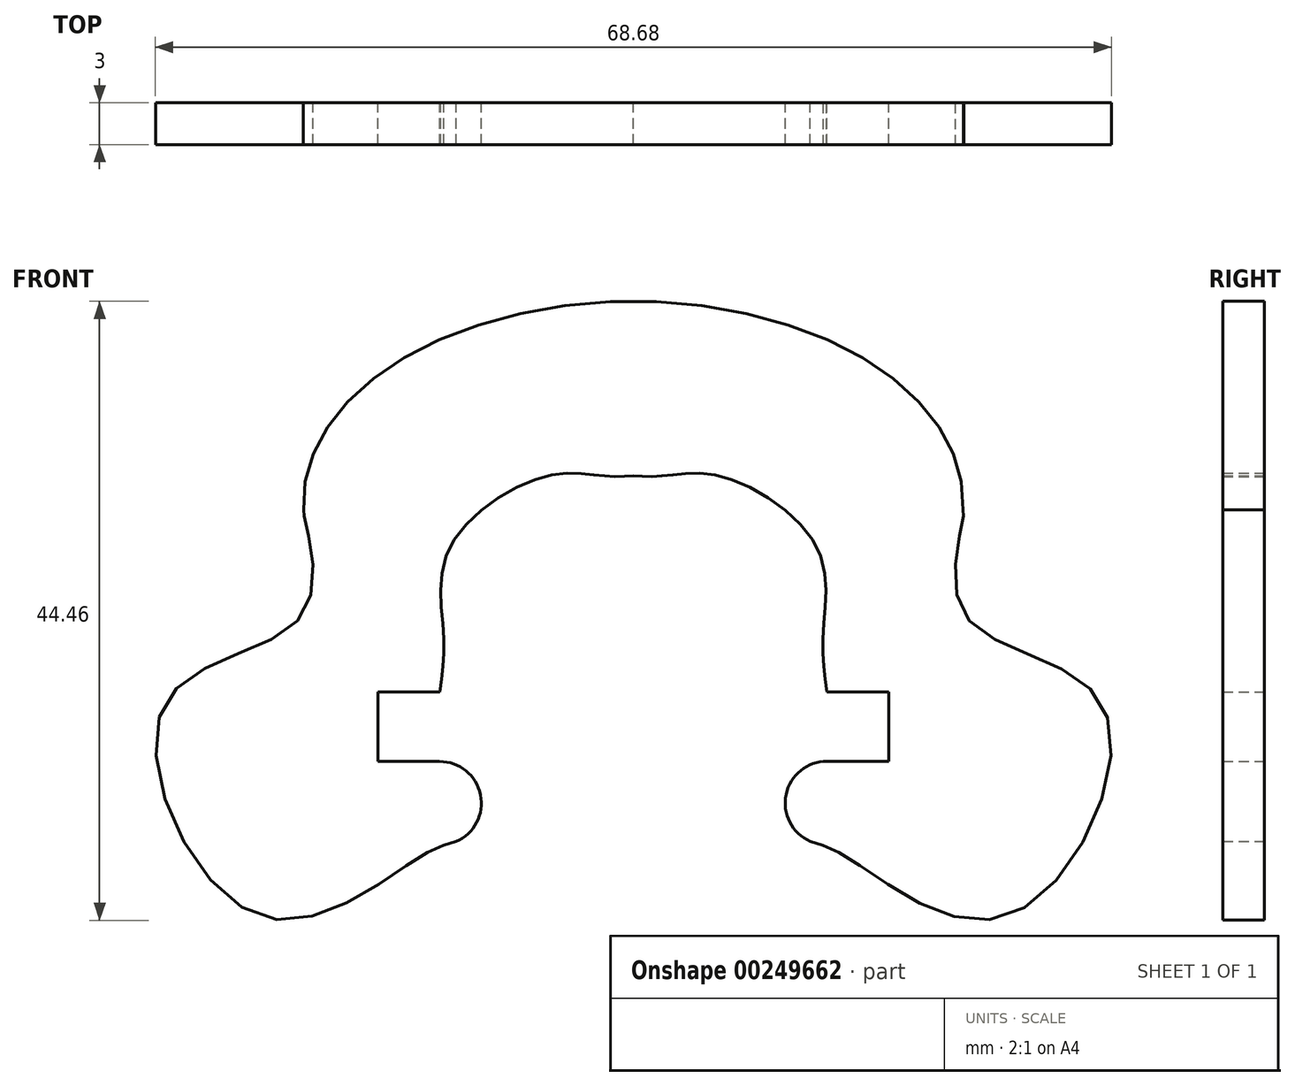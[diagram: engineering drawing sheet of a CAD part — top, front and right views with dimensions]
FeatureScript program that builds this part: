
annotation { "Feature Type Name" : "Feature", "Feature Type Description" : "" }
export const myFeature = defineFeature(function(context is Context, id is Id, definition is map)
    precondition{}
    {
        {
            var Q0;
            Q0=qCreatedBy(makeId("Front.planeOp"),FACE);
            var sketch = newSketch(context, id + "F0", { "sketchPlane" : qUnion([Q0])});
            skLineSegment(sketch, "E0", {"start": v(-18.36, -12.4) * mm, "end": v(-18.36, -7.4) * mm});
            skFitSpline(sketch, "E1", {"points": [v(-13.92, -7.4) * mm, v(-13.64, -3.33) * mm, v(-13.2, 2.92) * mm, v(-6.22, 8.09) * mm, v(-2.06, 8.1) * mm, v(0, 8.1) * mm]});
            skFitSpline(sketch, "E2", {"points": [v(13.91, -7.4) * mm, v(13.63, -3.33) * mm, v(13.2, 2.92) * mm, v(6.22, 8.09) * mm, v(2.06, 8.1) * mm, v(0, 8.1) * mm]});
            skLineSegment(sketch, "E3", {"start": v(18.35, -12.4) * mm, "end": v(18.35, -7.4) * mm});
            skLineSegment(sketch, "E4", {"start": v(18.35, -7.4) * mm, "end": v(13.91, -7.4) * mm});
            skLineSegment(sketch, "E5", {"start": v(-13.92, -7.4) * mm, "end": v(-18.36, -7.4) * mm});
            skEllipticalArc(sketch, "E6", {});
            skLineSegment(sketch, "E7", {"start": v(-18.36, -12.4) * mm, "end": v(-13.92, -12.4) * mm});
            skFitSpline(sketch, "E8", {"points": [v(-23.7, 5.68) * mm, v(-23.67, 5.35) * mm, v(-23.7, -1.75) * mm, v(-33.77, -8.43) * mm, v(-26.88, -23.48) * mm, v(-15.49, -19.35) * mm, v(-12.73, -18.16) * mm]});
            skArc(sketch, "E9", {"start": v(-12.73, -18.16) * mm, "mid": v(-10.98, -14.8) * mm, "end": v(-13.92, -12.4) * mm});
            skLineSegment(sketch, "E10", {"start": v(18.35, -12.4) * mm, "end": v(13.92, -12.39) * mm});
            skFitSpline(sketch, "E11", {"points": [v(23.69, 5.68) * mm, v(23.75, 5.33) * mm, v(23.74, -1.77) * mm, v(33.78, -8.5) * mm, v(26.83, -23.51) * mm, v(15.45, -19.34) * mm, v(12.7, -18.14) * mm]});
            skArc(sketch, "E12", {"start": v(13.92, -12.39) * mm, "mid": v(10.97, -14.77) * mm, "end": v(12.7, -18.14) * mm});
            const initialGuessF0  = {"E6": [-1.8649999997251144e-06, 0.006180337000000009, 23.703762, 0, 0.023703762000000003, 0.014459315, 6.248471, 9.459492]};
            skSetInitialGuess(sketch, initialGuessF0);
            skSolve(sketch);
        }
        {
            var Q0;
            Q0 = qSketchRegion(id + "F0", true);
            extrude(context, id + "F1", {"entities" : qUnion([Q0]), "depth" : 3 * mm});
        }
    });
